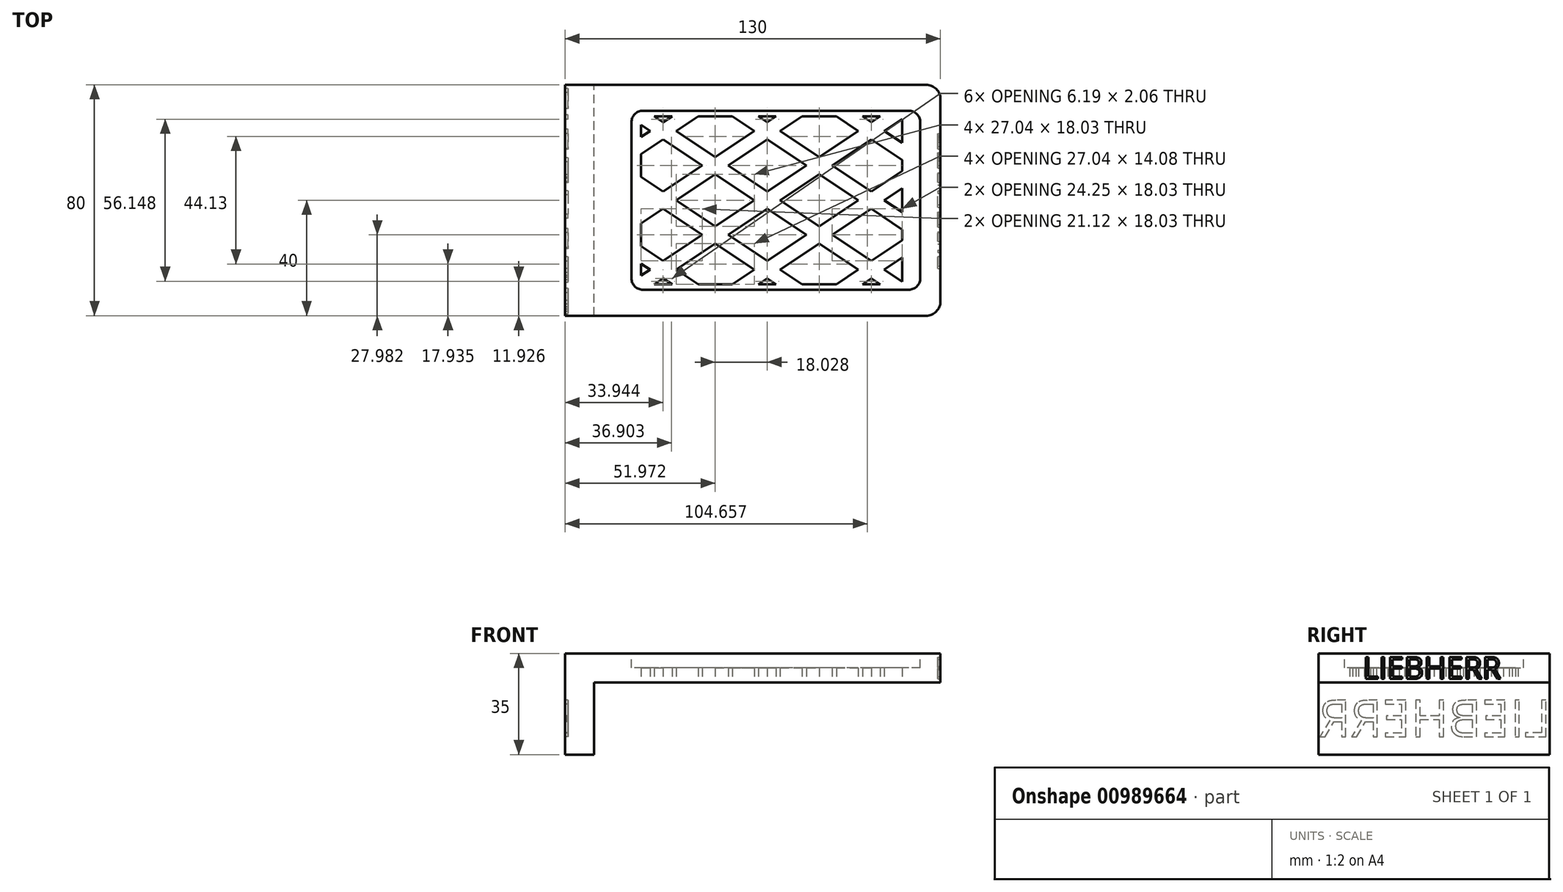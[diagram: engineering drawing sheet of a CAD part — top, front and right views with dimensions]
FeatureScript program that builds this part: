
annotation { "Feature Type Name" : "Feature", "Feature Type Description" : "" }
export const myFeature = defineFeature(function(context is Context, id is Id, definition is map)
    precondition{}
    {
        {
            var Q0;
            Q0=qCreatedBy(makeId("Top.planeOp"),FACE);
            var sketch = newSketch(context, id + "F0", { "sketchPlane" : qUnion([Q0])});
            skLineSegment(sketch, "E0.bottom", {"start": v(0, 0) * mm, "end": v(130, 0) * mm});
            skLineSegment(sketch, "E0.top", {"start": v(0, 80) * mm, "end": v(130, 80) * mm});
            skLineSegment(sketch, "E0.left", {"start": v(0, 0) * mm, "end": v(0, 80) * mm});
            skLineSegment(sketch, "E0.right", {"start": v(130, 0) * mm, "end": v(130, 80) * mm});
            skSolve(sketch);
        }
        {
            var Q0;
            Q0 = qSketchRegion(id + "F0", true);
            extrude(context, id + "F1", {"entities" : qUnion([Q0]), "depth" : 10 * mm, "offsetDistance" : 25 * mm});
        }
        {
            var Q0;
            Q0=makeQuery(id+"F1.opExtrude","CAP_FACE",FACE,{"disambiguationData":[OSD([sQuery(id+"F0.wireOp",EDGE,"E0.bottom"),sQuery(id+"F0.wireOp",EDGE,"E0.top"),sQuery(id+"F0.wireOp",EDGE,"E0.left"),sQuery(id+"F0.wireOp",EDGE,"E0.right")])],"isStart":false});
            var sketch = newSketch(context, id + "F2", { "sketchPlane" : qUnion([Q0])});
            skLineSegment(sketch, "E1.bottom", {"start": v(119, 71) * mm, "end": v(27, 71) * mm});
            skLineSegment(sketch, "E1.top", {"start": v(119, 9) * mm, "end": v(27, 9) * mm});
            skLineSegment(sketch, "E1.left", {"start": v(123, 67) * mm, "end": v(123, 13) * mm});
            skLineSegment(sketch, "E1.right", {"start": v(23, 67) * mm, "end": v(23, 13) * mm});
            skPoint(sketch, "E1.middle", {"position": v(73, 40) * mm});
            skPoint(sketch, "E1.middle.positionSnap0", {"position": v(0, 40) * mm});
            skPoint(sketch, "E1.middle.positionSnap1", {"position": v(65, 80) * mm});
            skPoint(sketch, "E1.centerSnap0", {"position": v(0, 40) * mm});
            skPoint(sketch, "E1.centerSnap1", {"position": v(65, 80) * mm});
            skPoint(sketch, "E2.visualSharp", {"position": v(23, 71) * mm});
            skArc(sketch, "E2.filletArc", {"start": v(27, 71) * mm, "mid": v(24.17, 69.83) * mm, "end": v(23, 67) * mm});
            skPoint(sketch, "E3.visualSharp", {"position": v(123, 71) * mm});
            skArc(sketch, "E3.filletArc", {"start": v(123, 67) * mm, "mid": v(121.83, 69.83) * mm, "end": v(119, 71) * mm});
            skPoint(sketch, "E4.visualSharp", {"position": v(123, 9) * mm});
            skArc(sketch, "E4.filletArc", {"start": v(119, 9) * mm, "mid": v(121.83, 10.17) * mm, "end": v(123, 13) * mm});
            skPoint(sketch, "E5.visualSharp", {"position": v(23, 9) * mm});
            skArc(sketch, "E5.filletArc", {"start": v(23, 13) * mm, "mid": v(24.17, 10.17) * mm, "end": v(27, 9) * mm});
            skLineSegment(sketch, "E6", {"start": v(0, 80) * mm, "end": v(73, 80) * mm, "construction": true});
            skLineSegment(sketch, "E7", {"start": v(73, 80) * mm, "end": v(73, 40) * mm, "construction": true});
            skSolve(sketch);
        }
        {
            var Q0;
            Q0 = qSketchRegion(id + "F2", true);
            extrude(context, id + "F3", {"entities" : qUnion([Q0]), "operationType" : NewBodyOperationType.REMOVE, "oppositeDirection" : true, "depth" : 5 * mm, "offsetDistance" : 25 * mm});
        }
        {
            var Q0;
            Q0=makeQuery(id+"F1.opExtrude","CAP_FACE",FACE,{"disambiguationData":[OSD([sQuery(id+"F0.wireOp",EDGE,"E0.bottom"),sQuery(id+"F0.wireOp",EDGE,"E0.top"),sQuery(id+"F0.wireOp",EDGE,"E0.left"),sQuery(id+"F0.wireOp",EDGE,"E0.right")])],"isStart":true});
            var sketch = newSketch(context, id + "F4", { "sketchPlane" : qUnion([Q0])});
            skLineSegment(sketch, "E8.bottom", {"start": v(0, 0) * mm, "end": v(10, 0) * mm});
            skLineSegment(sketch, "E8.top", {"start": v(0, -80) * mm, "end": v(10, -80) * mm});
            skLineSegment(sketch, "E8.left", {"start": v(0, 0) * mm, "end": v(0, -80) * mm});
            skLineSegment(sketch, "E8.right", {"start": v(10, 0) * mm, "end": v(10, -80) * mm});
            skSolve(sketch);
        }
        {
            var Q0;
            Q0 = qSketchRegion(id + "F4", true);
            extrude(context, id + "F5", {"entities" : qUnion([Q0]), "operationType" : NewBodyOperationType.ADD, "depth" : 25 * mm, "offsetDistance" : 25 * mm});
        }
        {
            var Q0;
            Q0=makeQuery(id+"F5.boolean.opBoolean","MERGE",FACE,{"derivedFrom":[makeQuery(id+"F1.opExtrude","SWEPT_FACE",FACE,{"disambiguationData":[OSD([sQuery(id+"F0.wireOp",EDGE,"E0.left")])]}),makeQuery(id+"F5.opExtrude","SWEPT_FACE",FACE,{"disambiguationData":[OSD([sQuery(id+"F4.wireOp",EDGE,"E8.left")])]})]});
            var sketch = newSketch(context, id + "F6", { "sketchPlane" : qUnion([Q0])});
            skText(sketch, "E9", { "text": "LIEBHERR", "fontName": "OpenSans-Regular.ttf"});
            const initialGuessF6  = {"E9": [-0.08046, -0.01882, 1, 0, 0.01274]};
            skSetInitialGuess(sketch, initialGuessF6);
            skSolve(sketch);
        }
        {
            var Q0;
            Q0 = qSketchRegion(id + "F6", true);
            extrude(context, id + "F7", {"entities" : qUnion([Q0]), "operationType" : NewBodyOperationType.REMOVE, "oppositeDirection" : true, "depth" : 1 * mm, "offsetDistance" : 25 * mm});
        }
        {
            var Q0;
            Q0=makeQuery(id+"F1.opExtrude","SWEPT_FACE",FACE,{"disambiguationData":[OSD([sQuery(id+"F0.wireOp",EDGE,"E0.right")])]});
            var sketch = newSketch(context, id + "F8", { "sketchPlane" : qUnion([Q0])});
            skText(sketch, "E10", { "text": "LIEBHERR", "fontName": "OpenSans-Regular.ttf"});
            const initialGuessF8  = {"E10": [0.01537, 0.00125, 1, 0, 0.0076]};
            skSetInitialGuess(sketch, initialGuessF8);
            skSolve(sketch);
        }
        {
            var Q0;
            Q0 = qSketchRegion(id + "F8", true);
            extrude(context, id + "F9", {"entities" : qUnion([Q0]), "operationType" : NewBodyOperationType.REMOVE, "oppositeDirection" : true, "depth" : 1 * mm, "offsetDistance" : 25 * mm});
        }
        {
            var Q0;
            Q0=makeQuery(id+"F1.opExtrude","CAP_FACE",FACE,{"disambiguationData":[OSD([sQuery(id+"F0.wireOp",EDGE,"E0.bottom"),sQuery(id+"F0.wireOp",EDGE,"E0.top"),sQuery(id+"F0.wireOp",EDGE,"E0.left"),sQuery(id+"F0.wireOp",EDGE,"E0.right")])],"isStart":true});
            var sketch = newSketch(context, id + "F10", { "sketchPlane" : qUnion([Q0])});
            skLineSegment(sketch, "E11", {"start": v(10, -80) * mm, "end": v(130, 0) * mm, "construction": true});
            skLineSegment(sketch, "E12", {"start": v(10, -55.96) * mm, "end": v(93.94, 0) * mm, "construction": true});
            skLineSegment(sketch, "E13", {"start": v(10, -7.89) * mm, "end": v(21.83, 0) * mm, "construction": true});
            skLineSegment(sketch, "E14", {"start": v(10, -31.93) * mm, "end": v(57.89, 0) * mm, "construction": true});
            skLineSegment(sketch, "E15", {"start": v(46.06, -80) * mm, "end": v(130, -24.04) * mm, "construction": true});
            skLineSegment(sketch, "E16", {"start": v(118.17, -80) * mm, "end": v(130, -72.11) * mm, "construction": true});
            skLineSegment(sketch, "E17", {"start": v(82.11, -80) * mm, "end": v(130, -48.07) * mm, "construction": true});
            skLineSegment(sketch, "E18", {"start": v(130, -80) * mm, "end": v(10, 0) * mm, "construction": true});
            skLineSegment(sketch, "E19", {"start": v(130, -55.96) * mm, "end": v(46.06, 0) * mm, "construction": true});
            skLineSegment(sketch, "E20", {"start": v(130, -31.93) * mm, "end": v(82.11, 0) * mm, "construction": true});
            skLineSegment(sketch, "E21", {"start": v(130, -7.89) * mm, "end": v(118.17, 0) * mm, "construction": true});
            skLineSegment(sketch, "E22", {"start": v(93.94, -80) * mm, "end": v(10, -24.04) * mm, "construction": true});
            skLineSegment(sketch, "E23", {"start": v(57.89, -80) * mm, "end": v(10, -48.07) * mm, "construction": true});
            skLineSegment(sketch, "E24", {"start": v(21.83, -80) * mm, "end": v(10, -72.11) * mm, "construction": true});
            skLineSegment(sketch, "E25.0", {"start": v(131.39, -77.92) * mm, "end": v(11.39, 2.08) * mm});
            skLineSegment(sketch, "E26.0", {"start": v(128.61, -82.08) * mm, "end": v(8.61, -2.08) * mm});
            skLineSegment(sketch, "E27.0", {"start": v(95.33, -77.92) * mm, "end": v(11.39, -21.96) * mm});
            skLineSegment(sketch, "E28.0", {"start": v(92.56, -82.08) * mm, "end": v(8.61, -26.12) * mm});
            skLineSegment(sketch, "E29.0", {"start": v(59.28, -77.92) * mm, "end": v(11.39, -46) * mm});
            skLineSegment(sketch, "E30.0", {"start": v(56.5, -82.08) * mm, "end": v(8.61, -50.15) * mm});
            skLineSegment(sketch, "E31.0", {"start": v(131.39, -53.88) * mm, "end": v(47.44, 2.08) * mm});
            skLineSegment(sketch, "E32.0", {"start": v(128.61, -58.04) * mm, "end": v(44.67, -2.08) * mm});
            skLineSegment(sketch, "E33.0", {"start": v(131.39, -29.85) * mm, "end": v(83.5, 2.08) * mm});
            skLineSegment(sketch, "E34.0", {"start": v(128.61, -34) * mm, "end": v(80.72, -2.08) * mm});
            skLineSegment(sketch, "E35.0", {"start": v(131.39, -5.8) * mm, "end": v(119.55, 2.08) * mm});
            skLineSegment(sketch, "E36.0", {"start": v(128.61, -9.97) * mm, "end": v(116.78, -2.08) * mm});
            skLineSegment(sketch, "E37.0", {"start": v(11.39, -34) * mm, "end": v(59.28, -2.08) * mm});
            skLineSegment(sketch, "E38.0", {"start": v(8.61, -29.85) * mm, "end": v(56.5, 2.08) * mm});
            skLineSegment(sketch, "E39.0", {"start": v(11.39, -9.97) * mm, "end": v(23.22, -2.08) * mm});
            skLineSegment(sketch, "E40.0", {"start": v(8.61, -5.8) * mm, "end": v(20.45, 2.08) * mm});
            skLineSegment(sketch, "E41.0", {"start": v(11.39, -58.04) * mm, "end": v(95.33, -2.08) * mm});
            skLineSegment(sketch, "E42.0", {"start": v(8.61, -53.88) * mm, "end": v(92.56, 2.08) * mm});
            skLineSegment(sketch, "E43.0", {"start": v(11.39, -82.08) * mm, "end": v(131.39, -2.08) * mm});
            skLineSegment(sketch, "E44.0", {"start": v(8.61, -77.92) * mm, "end": v(128.61, 2.08) * mm});
            skLineSegment(sketch, "E45.0", {"start": v(47.44, -82.08) * mm, "end": v(131.39, -26.12) * mm});
            skLineSegment(sketch, "E46.0", {"start": v(44.67, -77.92) * mm, "end": v(128.61, -21.96) * mm});
            skLineSegment(sketch, "E47.0", {"start": v(83.5, -82.08) * mm, "end": v(131.39, -50.15) * mm});
            skLineSegment(sketch, "E48.0", {"start": v(80.72, -77.92) * mm, "end": v(128.61, -46) * mm});
            skLineSegment(sketch, "E49.0", {"start": v(119.55, -82.08) * mm, "end": v(131.39, -74.2) * mm});
            skLineSegment(sketch, "E50.0", {"start": v(116.78, -77.92) * mm, "end": v(128.61, -70.03) * mm});
            skLineSegment(sketch, "E51", {"start": v(128.61, -70.03) * mm, "end": v(130, -69.1) * mm});
            skLineSegment(sketch, "E52", {"start": v(116.78, -77.92) * mm, "end": v(113.66, -80) * mm});
            skLineSegment(sketch, "E53", {"start": v(128.61, -46) * mm, "end": v(130, -45.07) * mm});
            skLineSegment(sketch, "E54", {"start": v(80.72, -77.92) * mm, "end": v(77.6, -80) * mm});
            skLineSegment(sketch, "E55", {"start": v(128.61, -34) * mm, "end": v(130, -34.93) * mm});
            skLineSegment(sketch, "E56", {"start": v(59.28, -77.92) * mm, "end": v(62.4, -80) * mm});
            skLineSegment(sketch, "E57", {"start": v(44.67, -77.92) * mm, "end": v(41.55, -80) * mm});
            skLineSegment(sketch, "E58", {"start": v(10, -72.11) * mm, "end": v(21.83, -80) * mm});
            skLineSegment(sketch, "E59", {"start": v(11.39, -58.04) * mm, "end": v(10, -58.97) * mm});
            skLineSegment(sketch, "E60", {"start": v(11.39, -46) * mm, "end": v(10, -45.07) * mm});
            skLineSegment(sketch, "E61", {"start": v(11.39, -21.96) * mm, "end": v(10, -21.03) * mm});
            skLineSegment(sketch, "E62", {"start": v(11.39, -9.97) * mm, "end": v(10, -10.9) * mm});
            skLineSegment(sketch, "E63", {"start": v(23.22, -2.08) * mm, "end": v(26.34, 0) * mm});
            skLineSegment(sketch, "E64", {"start": v(44.67, -2.08) * mm, "end": v(41.55, 0) * mm});
            skLineSegment(sketch, "E65", {"start": v(59.28, -2.08) * mm, "end": v(62.4, 0) * mm});
            skLineSegment(sketch, "E66", {"start": v(80.72, -2.08) * mm, "end": v(77.6, 0) * mm});
            skLineSegment(sketch, "E67", {"start": v(11.39, -34) * mm, "end": v(10, -34.93) * mm});
            skLineSegment(sketch, "E68", {"start": v(10, -10.9) * mm, "end": v(163.65, -10.9) * mm});
            skLineSegment(sketch, "E69", {"start": v(26.34, 0) * mm, "end": v(26.34, -91.53) * mm});
            skLineSegment(sketch, "E70", {"start": v(130, -69.1) * mm, "end": v(-37, -69.1) * mm});
            skLineSegment(sketch, "E71", {"start": v(116.78, -2.08) * mm, "end": v(116.78, -91.53) * mm});
            skSolve(sketch);
        }
        {
            var Q0;
            {var subQ0=sQuery(id+"F10.wireOp",EDGE,"E44.0");var subQ1=sQuery(id+"F10.wireOp",EDGE,"E28.0");var subQ2=makeQuery(id+"F10.imprint","INTERSECT",VERTEX,{"derivedFrom":[subQ1,subQ0]});Q0=makeQuery(id+"F10.imprint","IMPRINT",FACE,{"disambiguationData":[TD([[makeQuery(id+"F10.imprint","IMPRINT",EDGE,{"disambiguationData":[TD([[subQ2,-1.0]])],"derivedFrom":subQ1}),1.0]])]});}
            var Q1;
            {var subQ1=sQuery(id+"F10.wireOp",EDGE,"E28.0");var subQ7=sQuery(id+"F10.wireOp",EDGE,"E46.0");var subQ8=makeQuery(id+"F10.imprint","INTERSECT",VERTEX,{"derivedFrom":[subQ1,subQ7]});Q1=makeQuery(id+"F10.imprint","IMPRINT",FACE,{"disambiguationData":[TD([[makeQuery(id+"F10.imprint","IMPRINT",EDGE,{"disambiguationData":[TD([[subQ8,-1.0]])],"derivedFrom":subQ1}),1.0]])]});}
            var Q2;
            {var subQ0=sQuery(id+"F10.wireOp",EDGE,"E46.0");var subQ1=sQuery(id+"F10.wireOp",EDGE,"E26.0");var subQ2=makeQuery(id+"F10.imprint","INTERSECT",VERTEX,{"derivedFrom":[subQ1,subQ0]});Q2=makeQuery(id+"F10.imprint","IMPRINT",FACE,{"disambiguationData":[TD([[makeQuery(id+"F10.imprint","IMPRINT",EDGE,{"disambiguationData":[TD([[subQ2,-1.0]])],"derivedFrom":subQ1}),1.0]])]});}
            var Q3;
            {var subQ0=sQuery(id+"F10.wireOp",EDGE,"E42.0");var subQ1=sQuery(id+"F10.wireOp",EDGE,"E26.0");var subQ2=makeQuery(id+"F10.imprint","INTERSECT",VERTEX,{"derivedFrom":[subQ1,subQ0]});Q3=makeQuery(id+"F10.imprint","IMPRINT",FACE,{"disambiguationData":[TD([[makeQuery(id+"F10.imprint","IMPRINT",EDGE,{"disambiguationData":[TD([[subQ2,-1.0]])],"derivedFrom":subQ1}),1.0]])]});}
            var Q4;
            {var subQ1=sQuery(id+"F10.wireOp",EDGE,"E25.0");var subQ5=sQuery(id+"F10.wireOp",EDGE,"E42.0");var subQ6=makeQuery(id+"F10.imprint","INTERSECT",VERTEX,{"derivedFrom":[subQ1,subQ5]});Q4=makeQuery(id+"F10.imprint","IMPRINT",FACE,{"disambiguationData":[TD([[makeQuery(id+"F10.imprint","IMPRINT",EDGE,{"disambiguationData":[TD([[subQ6,-1.0]])],"derivedFrom":subQ1}),-1.0]])]});}
            var Q5;
            {var subQ0=sQuery(id+"F10.wireOp",EDGE,"E44.0");var subQ1=sQuery(id+"F10.wireOp",EDGE,"E26.0");var subQ2=makeQuery(id+"F10.imprint","INTERSECT",VERTEX,{"derivedFrom":[subQ1,subQ0]});Q5=makeQuery(id+"F10.imprint","IMPRINT",FACE,{"disambiguationData":[TD([[makeQuery(id+"F10.imprint","IMPRINT",EDGE,{"disambiguationData":[TD([[subQ2,-1.0]])],"derivedFrom":subQ1}),1.0]])]});}
            var Q6;
            {var subQ0=sQuery(id+"F10.wireOp",EDGE,"E44.0");var subQ1=sQuery(id+"F10.wireOp",EDGE,"E25.0");var subQ2=makeQuery(id+"F10.imprint","INTERSECT",VERTEX,{"derivedFrom":[subQ1,subQ0]});Q6=makeQuery(id+"F10.imprint","IMPRINT",FACE,{"disambiguationData":[TD([[makeQuery(id+"F10.imprint","IMPRINT",EDGE,{"disambiguationData":[TD([[subQ2,-1.0]])],"derivedFrom":subQ1}),-1.0]])]});}
            var Q7;
            {var subQ0=sQuery(id+"F10.wireOp",EDGE,"E44.0");var subQ1=sQuery(id+"F10.wireOp",EDGE,"E31.0");var subQ2=makeQuery(id+"F10.imprint","INTERSECT",VERTEX,{"derivedFrom":[subQ1,subQ0]});Q7=makeQuery(id+"F10.imprint","IMPRINT",FACE,{"disambiguationData":[TD([[makeQuery(id+"F10.imprint","IMPRINT",EDGE,{"disambiguationData":[TD([[subQ2,-1.0]])],"derivedFrom":subQ1}),-1.0]])]});}
            var Q8;
            {var subQ0=sQuery(id+"F10.wireOp",EDGE,"E71");var subQ1=sQuery(id+"F10.wireOp",EDGE,"E33.0");var subQ2=makeQuery(id+"F10.imprint","INTERSECT",VERTEX,{"derivedFrom":[subQ1,subQ0]});Q8=makeQuery(id+"F10.imprint","IMPRINT",FACE,{"disambiguationData":[TD([[makeQuery(id+"F10.imprint","IMPRINT",EDGE,{"disambiguationData":[TD([[subQ2,-1.0]])],"derivedFrom":subQ1}),-1.0]])]});}
            var Q9;
            {var subQ1=sQuery(id+"F10.wireOp",EDGE,"E31.0");var subQ7=sQuery(id+"F10.wireOp",EDGE,"E46.0");var subQ9=makeQuery(id+"F10.imprint","INTERSECT",VERTEX,{"derivedFrom":[subQ1,subQ7]});Q9=makeQuery(id+"F10.imprint","IMPRINT",FACE,{"disambiguationData":[TD([[makeQuery(id+"F10.imprint","IMPRINT",EDGE,{"disambiguationData":[TD([[subQ9,-1.0]])],"derivedFrom":subQ1}),-1.0]])]});}
            var Q10;
            {var subQ0=sQuery(id+"F10.wireOp",EDGE,"E46.0");var subQ1=sQuery(id+"F10.wireOp",EDGE,"E25.0");var subQ2=makeQuery(id+"F10.imprint","INTERSECT",VERTEX,{"derivedFrom":[subQ1,subQ0]});Q10=makeQuery(id+"F10.imprint","IMPRINT",FACE,{"disambiguationData":[TD([[makeQuery(id+"F10.imprint","IMPRINT",EDGE,{"disambiguationData":[TD([[subQ2,-1.0]])],"derivedFrom":subQ1}),-1.0]])]});}
            var Q11;
            {var subQ0=sQuery(id+"F10.wireOp",EDGE,"E71");var subQ1=sQuery(id+"F10.wireOp",EDGE,"E31.0");var subQ2=makeQuery(id+"F10.imprint","INTERSECT",VERTEX,{"derivedFrom":[subQ1,subQ0]});Q11=makeQuery(id+"F10.imprint","IMPRINT",FACE,{"disambiguationData":[TD([[makeQuery(id+"F10.imprint","IMPRINT",EDGE,{"disambiguationData":[TD([[subQ2,-1.0]])],"derivedFrom":subQ1}),-1.0]])]});}
            var Q12;
            {var subQ0=sQuery(id+"F10.wireOp",EDGE,"E48.0");var subQ1=sQuery(id+"F10.wireOp",EDGE,"E25.0");var subQ2=makeQuery(id+"F10.imprint","INTERSECT",VERTEX,{"derivedFrom":[subQ1,subQ0]});Q12=makeQuery(id+"F10.imprint","IMPRINT",FACE,{"disambiguationData":[TD([[makeQuery(id+"F10.imprint","IMPRINT",EDGE,{"disambiguationData":[TD([[subQ2,-1.0]])],"derivedFrom":subQ1}),-1.0]])]});}
            var Q13;
            {var subQ0=sQuery(id+"F10.wireOp",EDGE,"E48.0");var subQ1=sQuery(id+"F10.wireOp",EDGE,"E26.0");var subQ2=makeQuery(id+"F10.imprint","INTERSECT",VERTEX,{"derivedFrom":[subQ1,subQ0]});Q13=makeQuery(id+"F10.imprint","IMPRINT",FACE,{"disambiguationData":[TD([[makeQuery(id+"F10.imprint","IMPRINT",EDGE,{"disambiguationData":[TD([[subQ2,-1.0]])],"derivedFrom":subQ1}),1.0]])]});}
            var Q14;
            {var subQ0=sQuery(id+"F10.wireOp",EDGE,"E71");var subQ1=sQuery(id+"F10.wireOp",EDGE,"E25.0");var subQ2=makeQuery(id+"F10.imprint","INTERSECT",VERTEX,{"derivedFrom":[subQ1,subQ0]});Q14=makeQuery(id+"F10.imprint","IMPRINT",FACE,{"disambiguationData":[TD([[makeQuery(id+"F10.imprint","IMPRINT",EDGE,{"disambiguationData":[TD([[subQ2,-1.0]])],"derivedFrom":subQ1}),-1.0]])]});}
            var Q15;
            {var subQ0=sQuery(id+"F10.wireOp",EDGE,"E70");var subQ1=sQuery(id+"F10.wireOp",EDGE,"E26.0");var subQ2=makeQuery(id+"F10.imprint","INTERSECT",VERTEX,{"derivedFrom":[subQ1,subQ0]});Q15=makeQuery(id+"F10.imprint","IMPRINT",FACE,{"disambiguationData":[TD([[makeQuery(id+"F10.imprint","IMPRINT",EDGE,{"disambiguationData":[TD([[subQ2,-1.0]])],"derivedFrom":subQ1}),1.0]])]});}
            var Q16;
            {var subQ0=sQuery(id+"F10.wireOp",EDGE,"E70");var subQ1=sQuery(id+"F10.wireOp",EDGE,"E30.0");var subQ2=makeQuery(id+"F10.imprint","INTERSECT",VERTEX,{"derivedFrom":[subQ1,subQ0]});Q16=makeQuery(id+"F10.imprint","IMPRINT",FACE,{"disambiguationData":[TD([[makeQuery(id+"F10.imprint","IMPRINT",EDGE,{"disambiguationData":[TD([[subQ2,-1.0]])],"derivedFrom":subQ1}),1.0]])]});}
            var Q17;
            {var subQ0=sQuery(id+"F10.wireOp",EDGE,"E44.0");var subQ1=sQuery(id+"F10.wireOp",EDGE,"E30.0");var subQ2=makeQuery(id+"F10.imprint","INTERSECT",VERTEX,{"derivedFrom":[subQ1,subQ0]});Q17=makeQuery(id+"F10.imprint","IMPRINT",FACE,{"disambiguationData":[TD([[makeQuery(id+"F10.imprint","IMPRINT",EDGE,{"disambiguationData":[TD([[subQ2,-1.0]])],"derivedFrom":subQ1}),1.0]])]});}
            var Q18;
            {var subQ0=sQuery(id+"F10.wireOp",EDGE,"E38.0");var subQ1=sQuery(id+"F10.wireOp",EDGE,"E26.0");var subQ2=makeQuery(id+"F10.imprint","INTERSECT",VERTEX,{"derivedFrom":[subQ1,subQ0]});Q18=makeQuery(id+"F10.imprint","IMPRINT",FACE,{"disambiguationData":[TD([[makeQuery(id+"F10.imprint","IMPRINT",EDGE,{"disambiguationData":[TD([[subQ2,-1.0]])],"derivedFrom":subQ1}),1.0]])]});}
            var Q19;
            {var subQ0=sQuery(id+"F10.wireOp",EDGE,"E38.0");var subQ1=sQuery(id+"F10.wireOp",EDGE,"E25.0");var subQ2=makeQuery(id+"F10.imprint","INTERSECT",VERTEX,{"derivedFrom":[subQ1,subQ0]});Q19=makeQuery(id+"F10.imprint","IMPRINT",FACE,{"disambiguationData":[TD([[makeQuery(id+"F10.imprint","IMPRINT",EDGE,{"disambiguationData":[TD([[subQ2,-1.0]])],"derivedFrom":subQ1}),-1.0]])]});}
            var Q20;
            {var subQ0=sQuery(id+"F10.wireOp",EDGE,"E44.0");var subQ1=sQuery(id+"F10.wireOp",EDGE,"E33.0");var subQ2=makeQuery(id+"F10.imprint","INTERSECT",VERTEX,{"derivedFrom":[subQ1,subQ0]});Q20=makeQuery(id+"F10.imprint","IMPRINT",FACE,{"disambiguationData":[TD([[makeQuery(id+"F10.imprint","IMPRINT",EDGE,{"disambiguationData":[TD([[subQ2,-1.0]])],"derivedFrom":subQ1}),-1.0]])]});}
            var Q21;
            {var subQ0=sQuery(id+"F10.wireOp",EDGE,"E70");var subQ1=sQuery(id+"F10.wireOp",EDGE,"E28.0");var subQ2=makeQuery(id+"F10.imprint","INTERSECT",VERTEX,{"derivedFrom":[subQ1,subQ0]});Q21=makeQuery(id+"F10.imprint","IMPRINT",FACE,{"disambiguationData":[TD([[makeQuery(id+"F10.imprint","IMPRINT",EDGE,{"disambiguationData":[TD([[subQ2,-1.0]])],"derivedFrom":subQ1}),1.0]])]});}
            var Q22;
            {var subQ0=sQuery(id+"F10.wireOp",EDGE,"E42.0");var subQ1=sQuery(id+"F10.wireOp",EDGE,"E31.0");var subQ2=makeQuery(id+"F10.imprint","INTERSECT",VERTEX,{"derivedFrom":[subQ1,subQ0]});Q22=makeQuery(id+"F10.imprint","IMPRINT",FACE,{"disambiguationData":[TD([[makeQuery(id+"F10.imprint","IMPRINT",EDGE,{"disambiguationData":[TD([[subQ2,-1.0]])],"derivedFrom":subQ1}),-1.0]])]});}
            extrude(context, id + "F11", {"entities" : qUnion([Q0, Q1, Q2, Q3, Q4, Q5, Q6, Q7, Q8, Q9, Q10, Q11, Q12, Q13, Q14, Q15, Q16, Q17, Q18, Q19, Q20, Q21, Q22]), "operationType" : NewBodyOperationType.REMOVE, "oppositeDirection" : true, "depth" : 25 * mm, "offsetDistance" : 25 * mm});
        }
        {
            var Q0;
            Q0=makeQuery(id+"F1.opExtrude","SWEPT_EDGE",EDGE,{"disambiguationData":[OSD([sQuery(id+"F0.wireOp",EDGE,"E0.bottom"),sQuery(id+"F0.wireOp",EDGE,"E0.right")])]});
            var Q1;
            Q1=makeQuery(id+"F1.opExtrude","SWEPT_EDGE",EDGE,{"disambiguationData":[OSD([sQuery(id+"F0.wireOp",EDGE,"E0.top"),sQuery(id+"F0.wireOp",EDGE,"E0.right")])]});
            fillet(context, id + "F12", {"entities" : qUnion([Q0, Q1]), "radius" : 5 * mm, "tangentPropagation" : true, "allowEdgeOverflow" : false});
        }
    });
